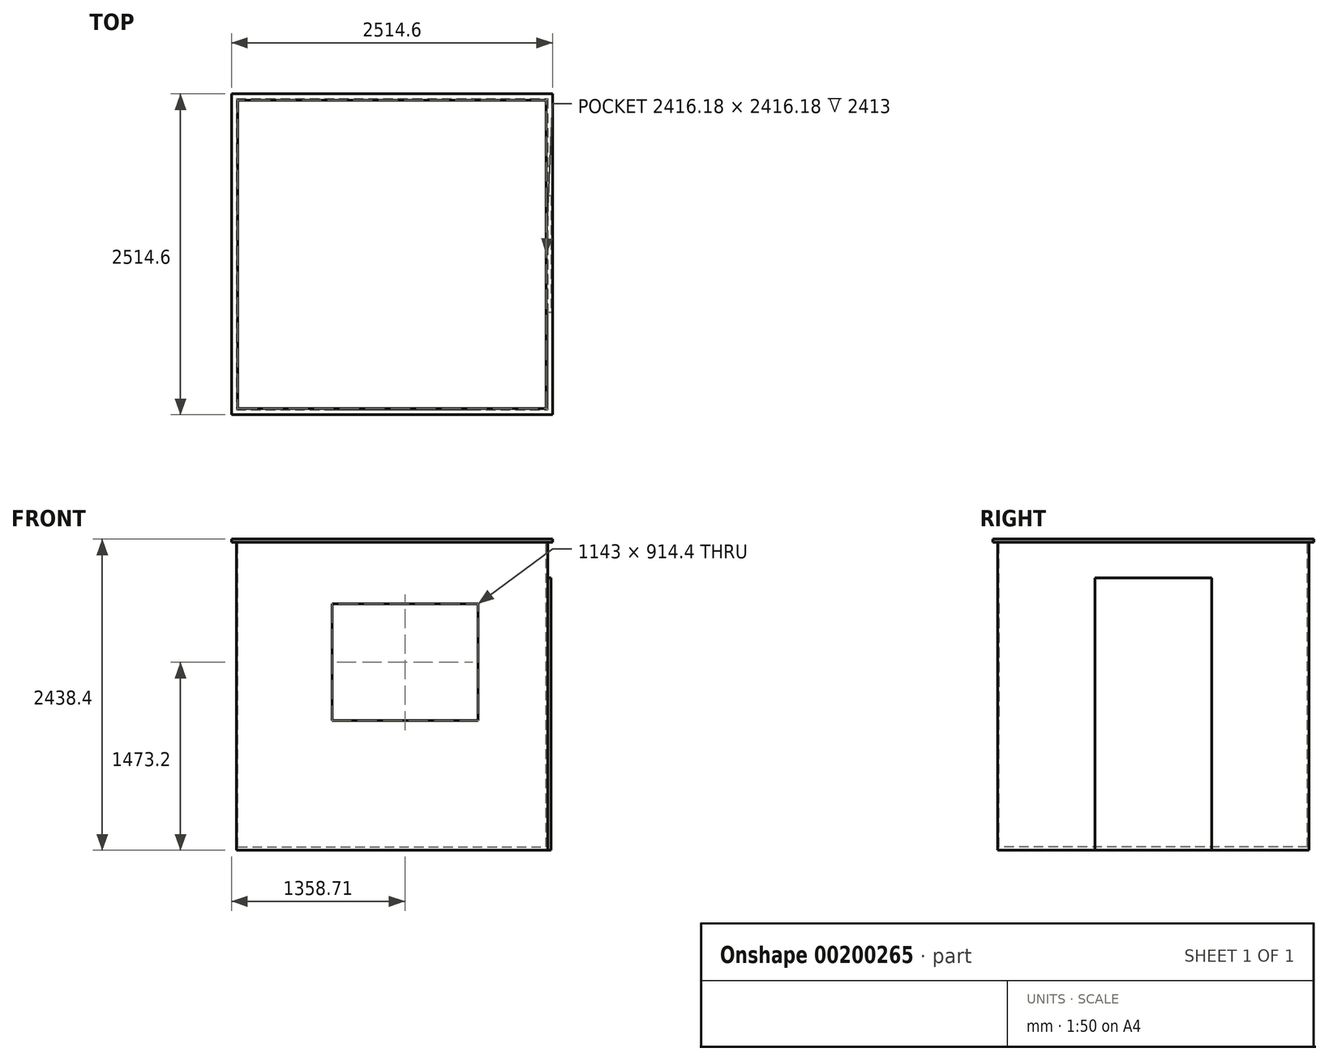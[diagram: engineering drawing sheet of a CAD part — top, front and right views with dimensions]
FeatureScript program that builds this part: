
annotation { "Feature Type Name" : "Feature", "Feature Type Description" : "" }
export const myFeature = defineFeature(function(context is Context, id is Id, definition is map)
    precondition{}
    {
        {
            var Q0;
            Q0=qCreatedBy(makeId("Top.planeOp"),FACE);
            var sketch = newSketch(context, id + "F0", { "sketchPlane" : qUnion([Q0])});
            skLineSegment(sketch, "E0.bottom", {"start": v(-1219.2, 1219.2) * mm, "end": v(1219.2, 1219.2) * mm});
            skLineSegment(sketch, "E0.top", {"start": v(-1219.2, -1219.2) * mm, "end": v(1219.2, -1219.2) * mm});
            skLineSegment(sketch, "E0.left", {"start": v(-1219.2, 1219.2) * mm, "end": v(-1219.2, -1219.2) * mm});
            skLineSegment(sketch, "E0.right", {"start": v(1219.2, 1219.2) * mm, "end": v(1219.2, -1219.2) * mm});
            skSolve(sketch);
        }
        {
            var Q0;
            Q0=makeQuery(id+"F0.imprint","IMPRINT",FACE,{"disambiguationData":[TD([[makeQuery(id+"F0.imprint","IMPRINT",EDGE,{"derivedFrom":sQuery(id+"F0.wireOp",EDGE,"E0.bottom")}),-1.0]])]});
            extrude(context, id + "F1", {"entities" : qUnion([Q0]), "depth" : 2438.4 * mm});
        }
        {
            var Q0;
            Q0=makeQuery(id+"F1.opExtrude","CAP_FACE",FACE,{"disambiguationData":[OSD([sQuery(id+"F0.wireOp",EDGE,"E0.bottom"),sQuery(id+"F0.wireOp",EDGE,"E0.top"),sQuery(id+"F0.wireOp",EDGE,"E0.left"),sQuery(id+"F0.wireOp",EDGE,"E0.right")])],"isStart":false});
            var sketch = newSketch(context, id + "F2", { "sketchPlane" : qUnion([Q0])});
            skLineSegment(sketch, "E1.bottom", {"start": v(-1208.09, 1208.09) * mm, "end": v(1208.09, 1208.09) * mm});
            skLineSegment(sketch, "E1.top", {"start": v(-1208.09, -1208.09) * mm, "end": v(1208.09, -1208.09) * mm});
            skLineSegment(sketch, "E1.left", {"start": v(-1208.09, 1208.09) * mm, "end": v(-1208.09, -1208.09) * mm});
            skLineSegment(sketch, "E1.right", {"start": v(1208.09, 1208.09) * mm, "end": v(1208.09, -1208.09) * mm});
            skSolve(sketch);
        }
        {
            var Q0;
            Q0=makeQuery(id+"F2.imprint","IMPRINT",FACE,{"disambiguationData":[TD([[makeQuery(id+"F2.imprint","IMPRINT",EDGE,{"derivedFrom":sQuery(id+"F2.wireOp",EDGE,"E1.bottom")}),-1.0]])]});
            extrude(context, id + "F3", {"entities" : qUnion([Q0]), "operationType" : NewBodyOperationType.REMOVE, "oppositeDirection" : true, "depth" : 2413 * mm});
        }
        {
            var Q0;
            Q0=makeQuery(id+"F1.opExtrude","SWEPT_FACE",FACE,{"disambiguationData":[OSD([sQuery(id+"F0.wireOp",EDGE,"E0.right")])]});
            var sketch = newSketch(context, id + "F4", { "sketchPlane" : qUnion([Q0])});
            skLineSegment(sketch, "E2.bottom", {"start": v(-457.2, 2133.6) * mm, "end": v(457.2, 2133.6) * mm});
            skLineSegment(sketch, "E2.top", {"start": v(-457.2, 0) * mm, "end": v(457.2, 0) * mm});
            skLineSegment(sketch, "E2.left", {"start": v(-457.2, 2133.6) * mm, "end": v(-457.2, 0) * mm});
            skLineSegment(sketch, "E2.right", {"start": v(457.2, 2133.6) * mm, "end": v(457.2, 0) * mm});
            skSolve(sketch);
        }
        {
            var Q0;
            Q0=makeQuery(id+"F4.imprint","IMPRINT",FACE,{"disambiguationData":[TD([[makeQuery(id+"F4.imprint","IMPRINT",EDGE,{"derivedFrom":sQuery(id+"F4.wireOp",EDGE,"E2.bottom")}),-1.0]])]});
            extrude(context, id + "F5", {"entities" : qUnion([Q0]), "operationType" : NewBodyOperationType.ADD, "depth" : 25.4 * mm});
        }
        {
            var Q0;
            Q0=makeQuery(id+"F1.opExtrude","SWEPT_FACE",FACE,{"disambiguationData":[OSD([sQuery(id+"F0.wireOp",EDGE,"E0.top")])]});
            var sketch = newSketch(context, id + "F6", { "sketchPlane" : qUnion([Q0])});
            skLineSegment(sketch, "E3.bottom", {"start": v(-470.1, 1930.4) * mm, "end": v(672.9, 1930.4) * mm});
            skLineSegment(sketch, "E3.top", {"start": v(-470.1, 1016) * mm, "end": v(672.9, 1016) * mm});
            skLineSegment(sketch, "E3.left", {"start": v(-470.1, 1930.4) * mm, "end": v(-470.1, 1016) * mm});
            skLineSegment(sketch, "E3.right", {"start": v(672.9, 1930.4) * mm, "end": v(672.9, 1016) * mm});
            skSolve(sketch);
        }
        {
            var Q0;
            Q0=makeQuery(id+"F6.imprint","IMPRINT",FACE,{"disambiguationData":[TD([[makeQuery(id+"F6.imprint","IMPRINT",EDGE,{"derivedFrom":sQuery(id+"F6.wireOp",EDGE,"E3.bottom")}),-1.0]])]});
            extrude(context, id + "F7", {"entities" : qUnion([Q0]), "operationType" : NewBodyOperationType.REMOVE, "oppositeDirection" : true, "depth" : 25.4 * mm});
        }
        {
            var Q0;
            Q0=makeQuery(id+"F1.opExtrude","CAP_FACE",FACE,{"disambiguationData":[OSD([sQuery(id+"F0.wireOp",EDGE,"E0.bottom"),sQuery(id+"F0.wireOp",EDGE,"E0.top"),sQuery(id+"F0.wireOp",EDGE,"E0.left"),sQuery(id+"F0.wireOp",EDGE,"E0.right")])],"isStart":false});
            var sketch = newSketch(context, id + "F8", { "sketchPlane" : qUnion([Q0])});
            skLineSegment(sketch, "E4.bottom", {"start": v(-1257.3, 1257.3) * mm, "end": v(1257.3, 1257.3) * mm});
            skLineSegment(sketch, "E4.top", {"start": v(-1257.3, -1257.3) * mm, "end": v(1257.3, -1257.3) * mm});
            skLineSegment(sketch, "E4.left", {"start": v(-1257.3, 1257.3) * mm, "end": v(-1257.3, -1257.3) * mm});
            skLineSegment(sketch, "E4.right", {"start": v(1257.3, 1257.3) * mm, "end": v(1257.3, -1257.3) * mm});
            skSolve(sketch);
        }
        {
            var Q0;
            Q0=makeQuery(id+"F8.imprint","IMPRINT",FACE,{"disambiguationData":[TD([[makeQuery(id+"F8.imprint","IMPRINT",EDGE,{"derivedFrom":makeQuery(id+"F3.boolean.opBoolean","COPY",EDGE,{"derivedFrom":makeQuery(id+"F3.opExtrude","CAP_EDGE",EDGE,{"disambiguationData":[OSD([sQuery(id+"F2.wireOp",EDGE,"E1.bottom")])],"isStart":true})})}),-1.0]])]});
            var Q1;
            Q1=makeQuery(id+"F8.imprint","IMPRINT",FACE,{"disambiguationData":[TD([[makeQuery(id+"F8.imprint","IMPRINT",EDGE,{"derivedFrom":sQuery(id+"F8.wireOp",EDGE,"E4.bottom")}),-1.0]])]});
            extrude(context, id + "F9", {"entities" : qUnion([Q0, Q1]), "operationType" : NewBodyOperationType.ADD, "oppositeDirection" : true, "depth" : 25.4 * mm});
        }
    });
